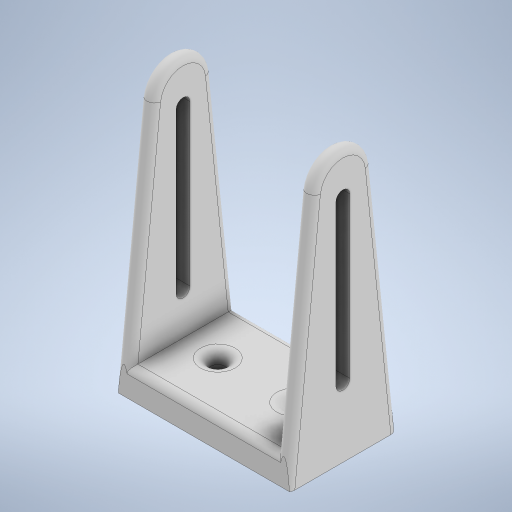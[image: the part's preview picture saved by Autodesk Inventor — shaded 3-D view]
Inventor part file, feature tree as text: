
AUTODESK INVENTOR PART (.ipt)
format: ipt  version: 2023 (Build 270158000, 158)  size: 723,968 bytes
history: native  units: mm
features: extrude x4, chamfer x4, fillet x4, sketch x4, other x1
ambient origin geometry x8: Origin, YZ Plane, XZ Plane, XY Plane, X Axis, Y Axis, Z Axis, Center Point
bodies: Body1 (feature_tree)
feature tree (17):
  other  "Bryła1"
  extrude  "Wyciągnięcie proste1"  Depth=50.0mm
  extrude  "Wyciągnięcie proste2"  Depth=30.0mm
  chamfer  "Faza1"  Distance=8.0mm
  chamfer  "Faza2"  Distance=4.0mm
  chamfer  "Faza3"  Distance=4.0mm
  chamfer  "Faza4"  Distance=70.0mm
  extrude  "Wyciągnięcie proste3"  Depth=2.0mm
  extrude  "Wyciągnięcie proste4"  Depth=2.0mm
  fillet  "Zaokrąglenie1"  Radius=2.0mm
  fillet  "Zaokrąglenie2"  Radius=2.0mm
  fillet  "Zaokrąglenie3"  Radius=4.0mm
  fillet  "Zaokrąglenie4"  Radius=10.040411mm
  sketch  "Szkic1"
  sketch  "Szkic2"
  sketch  "Szkic3"
  sketch  "Szkic4"
